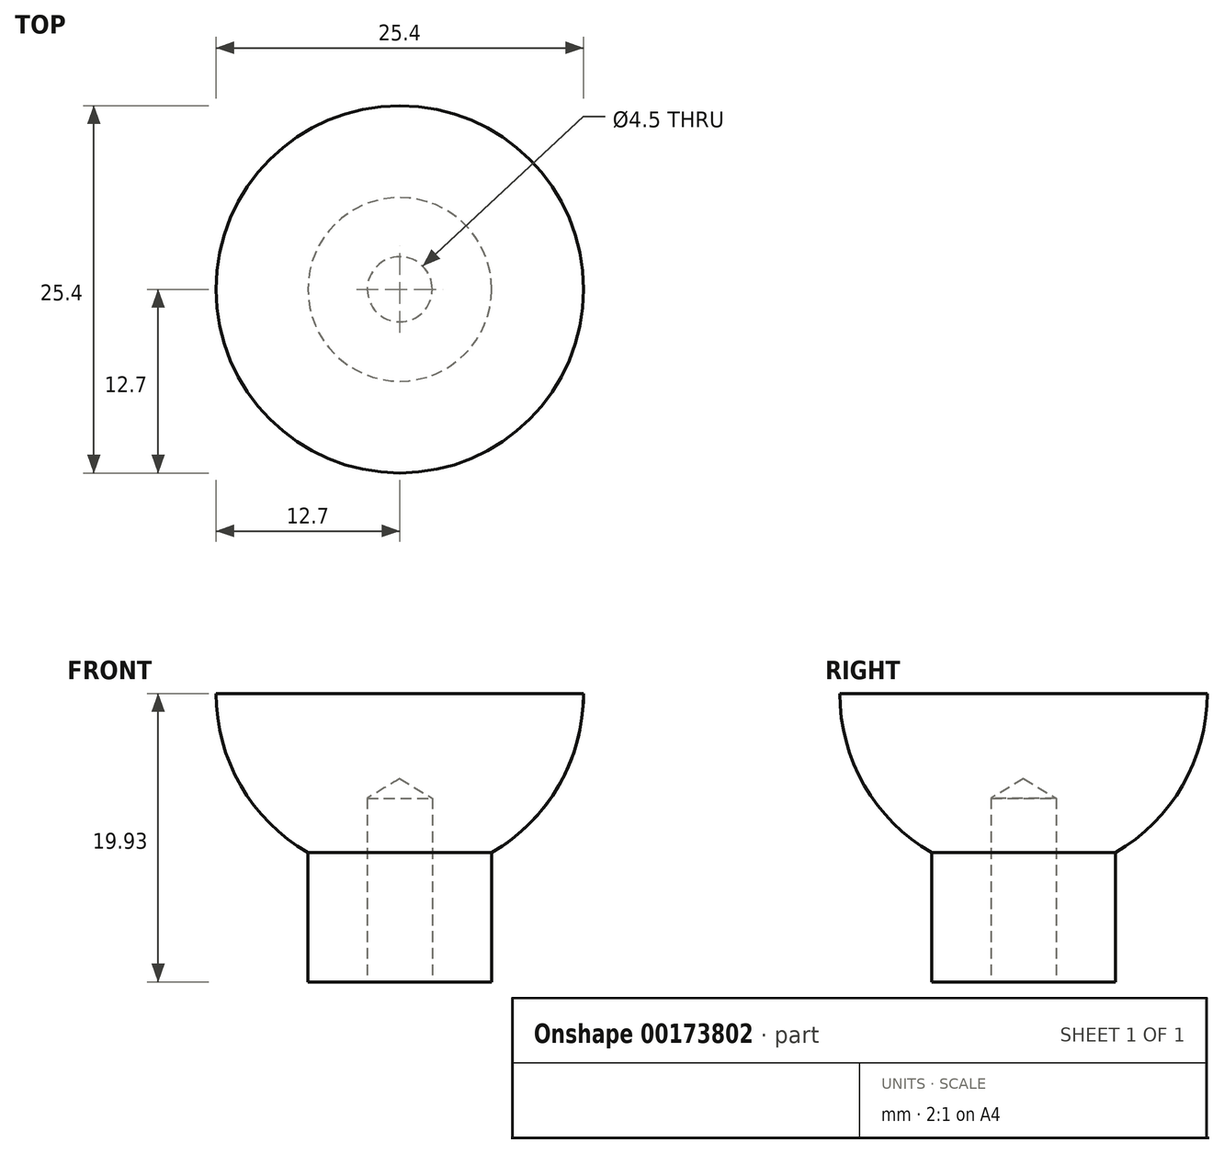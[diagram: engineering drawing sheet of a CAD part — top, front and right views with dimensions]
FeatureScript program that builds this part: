
annotation { "Feature Type Name" : "Feature", "Feature Type Description" : "" }
export const myFeature = defineFeature(function(context is Context, id is Id, definition is map)
    precondition{}
    {
        {
            var Q0;
            Q0=qCreatedBy(makeId("Right.planeOp"),FACE);
            var sketch = newSketch(context, id + "F0", { "sketchPlane" : qUnion([Q0])});
            skLineSegment(sketch, "E0", {"start": v(0, 0) * mm, "end": v(-6.35, 0) * mm});
            skLineSegment(sketch, "E1", {"start": v(-6.35, 0) * mm, "end": v(-6.35, 8.93) * mm});
            skArc(sketch, "E2", {"start": v(-12.7, 19.93) * mm, "mid": v(-11, 13.58) * mm, "end": v(-6.35, 8.93) * mm});
            skLineSegment(sketch, "E3", {"start": v(0, 19.93) * mm, "end": v(0, 7.23) * mm});
            skLineSegment(sketch, "E4", {"start": v(0, 7.23) * mm, "end": v(0, 0) * mm});
            skLineSegment(sketch, "E5", {"start": v(0, 19.93) * mm, "end": v(-12.7, 19.93) * mm});
            skPoint(sketch, "E6.orphan", {"position": v(0, 32.63) * mm});
            skSolve(sketch);
        }
        {
            var Q0;
            Q0 = qSketchRegion(id + "F0", true);
            var Q1;
            Q1=sQuery(id+"F0.wireOp",EDGE,"E3");
            revolve(context, id + "F1", {"entities" : qUnion([Q0]), "axis" : qUnion([Q1]), "revolveType" : RevolveType.FULL});
        }
        {
            var Q0;
            Q0=makeQuery(id+"F1.opRevolve","SWEPT_FACE",FACE,{"disambiguationData":[OSD([sQuery(id+"F0.wireOp",EDGE,"E0")])]});
            var sketch = newSketch(context, id + "F2", { "sketchPlane" : qUnion([Q0])});
            skPoint(sketch, "E7", {"position": v(0, 0) * mm});
            skSolve(sketch);
        }
        {
            var Q0;
            Q0=sQuery(id+"F2.wireOp",VERTEX,"E7");
            var Q1;
            Q1=makeQuery(id+"F1.opRevolve","SWEPT_BODY",BODY,{"disambiguationData":[OSD([sQuery(id+"F0.wireOp",EDGE,"E0"),sQuery(id+"F0.wireOp",EDGE,"E1"),sQuery(id+"F0.wireOp",EDGE,"E2"),sQuery(id+"F0.wireOp",EDGE,"E3"),sQuery(id+"F0.wireOp",EDGE,"E4")])]});
            hole(context, id + "F3", {"style" : HoleStyle.SIMPLE, "endStyle" : HoleEndStyle.BLIND, "standardTappedOrClearance" : lookupTablePath({ "standard" : "ANSI", "fit" : "Normal (ASME)", "size" : "#8", "type" : "Clearance" }), "standardBlindInLast" : lookupTablePath({ "fit" : "Free", "standard" : "ANSI", "size" : "#8", "type" : "Clearance" }), "holeDiameter" : 4.5 * mm, "holeDepth" : 12.7 * mm, "startFromSketch" : true, "locations" : qUnion([Q0]), "scope" : qUnion([Q1])});
        }
    });
